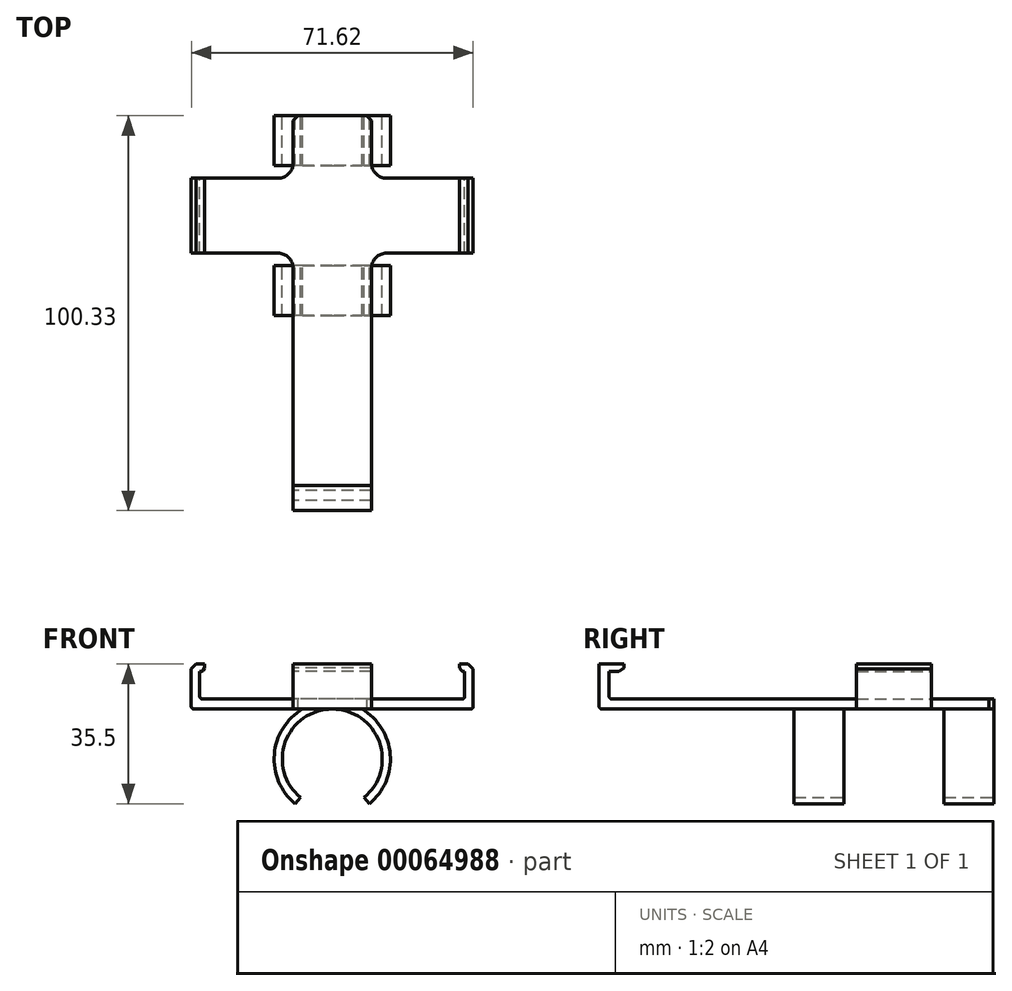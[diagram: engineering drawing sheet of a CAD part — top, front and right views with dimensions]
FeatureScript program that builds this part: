
annotation { "Feature Type Name" : "Feature", "Feature Type Description" : "" }
export const myFeature = defineFeature(function(context is Context, id is Id, definition is map)
    precondition{}
    {
        {
            var Q0;
            Q0=qCreatedBy(makeId("Front.planeOp"),FACE);
            var sketch = newSketch(context, id + "F0", { "sketchPlane" : qUnion([Q0])});
            skArc(sketch, "E0", {"start": v(9.41, -11.37) * mm, "mid": v(0, 14.76) * mm, "end": v(-9.41, -11.37) * mm});
            skArc(sketch, "E1", {"start": v(8.1, -9.78) * mm, "mid": v(0, 12.7) * mm, "end": v(-8.1, -9.78) * mm});
            skLineSegment(sketch, "E2", {"start": v(-8.1, -9.78) * mm, "end": v(-9.41, -11.37) * mm});
            skLineSegment(sketch, "E3", {"start": v(8.1, -9.78) * mm, "end": v(9.41, -11.37) * mm});
            skLineSegment(sketch, "E4", {"start": v(0, 0) * mm, "end": v(0, -14.76) * mm, "construction": true});
            skSolve(sketch);
        }
        {
            var Q0;
            Q0 = qSketchRegion(id + "F0", true);
            extrude(context, id + "F1", {"entities" : qUnion([Q0]), "depth" : 25.4 * mm, "hasSecondDirection" : true, "secondDirectionOppositeDirection" : true, "secondDirectionDepth" : 25.4 * mm});
        }
        {
            var Q0;
            Q0=qCreatedBy(makeId("Right.planeOp"),FACE);
            var sketch = newSketch(context, id + "F2", { "sketchPlane" : qUnion([Q0])});
            skLineSegment(sketch, "E5.bottom", {"start": v(-12.7, 21.65) * mm, "end": v(12.7, 21.65) * mm});
            skLineSegment(sketch, "E5.top", {"start": v(-12.7, -19.3) * mm, "end": v(12.7, -19.3) * mm});
            skLineSegment(sketch, "E5.left", {"start": v(-12.7, 21.65) * mm, "end": v(-12.7, -19.3) * mm});
            skLineSegment(sketch, "E5.right", {"start": v(12.7, 21.65) * mm, "end": v(12.7, -19.3) * mm});
            skSolve(sketch);
        }
        {
            var Q0;
            Q0 = qSketchRegion(id + "F2", true);
            extrude(context, id + "F3", {"entities" : qUnion([Q0]), "operationType" : NewBodyOperationType.REMOVE, "oppositeDirection" : true, "depth" : 25.4 * mm, "hasSecondDirection" : true, "secondDirectionOppositeDirection" : false, "secondDirectionDepth" : 25.4 * mm});
        }
        {
            var Q0;
            Q0=qCreatedBy(makeId("Front.planeOp"),FACE);
            var sketch = newSketch(context, id + "F4", { "sketchPlane" : qUnion([Q0])});
            skLineSegment(sketch, "E6", {"start": v(0, 12.7) * mm, "end": v(0, 14.76) * mm, "construction": true});
            skLineSegment(sketch, "E7.rect.bottom", {"start": v(9.97, 12.7) * mm, "end": v(-9.97, 12.7) * mm});
            skLineSegment(sketch, "E7.rect.top", {"start": v(9.97, 15.24) * mm, "end": v(-9.97, 15.24) * mm});
            skLineSegment(sketch, "E7.rect.left", {"start": v(9.97, 12.7) * mm, "end": v(9.97, 15.24) * mm});
            skLineSegment(sketch, "E7.rect.right", {"start": v(-9.97, 12.7) * mm, "end": v(-9.97, 15.24) * mm});
            skPoint(sketch, "E7.rect.middle", {"position": v(0, 13.97) * mm});
            skSolve(sketch);
        }
        {
            var Q0;
            Q0 = qSketchRegion(id + "F4", true);
            extrude(context, id + "F5", {"entities" : qUnion([Q0]), "operationType" : NewBodyOperationType.ADD, "depth" : 25.4 * mm, "hasSecondDirection" : true, "secondDirectionOppositeDirection" : true, "secondDirectionDepth" : 25.4 * mm});
        }
        {
            var Q0;
            Q0=qCreatedBy(makeId("Front.planeOp"),FACE);
            var sketch = newSketch(context, id + "F6", { "sketchPlane" : qUnion([Q0])});
            skLineSegment(sketch, "E8.rect.bottom", {"start": v(0, 12.7) * mm, "end": v(-33.66, 12.7) * mm});
            skLineSegment(sketch, "E8.rect.top", {"start": v(0, 15.24) * mm, "end": v(-33.02, 15.24) * mm});
            skPoint(sketch, "E8.rect.middle", {"position": v(0, 13.97) * mm});
            skLineSegment(sketch, "E9.bottom", {"start": v(-33.66, 12.7) * mm, "end": v(-35.18, 12.7) * mm});
            skLineSegment(sketch, "E9.left", {"start": v(-33.66, 15.87) * mm, "end": v(-33.65, 22.23) * mm});
            skLineSegment(sketch, "E9.right", {"start": v(-35.81, 13.33) * mm, "end": v(-35.81, 22.23) * mm});
            skPoint(sketch, "E10.visualSharp", {"position": v(-33.66, 15.24) * mm});
            skArc(sketch, "E10.filletArc", {"start": v(-33.66, 15.87) * mm, "mid": v(-33.47, 15.43) * mm, "end": v(-33.02, 15.24) * mm});
            skPoint(sketch, "E11.visualSharp", {"position": v(-35.81, 12.7) * mm});
            skArc(sketch, "E11.filletArc", {"start": v(-35.81, 13.33) * mm, "mid": v(-35.63, 12.89) * mm, "end": v(-35.18, 12.7) * mm});
            skLineSegment(sketch, "E12.bottom", {"start": v(-33.65, 22.23) * mm, "end": v(-33.36, 22.23) * mm});
            skLineSegment(sketch, "E12.top", {"start": v(-35.81, 24.13) * mm, "end": v(-32.39, 24.13) * mm});
            skLineSegment(sketch, "E12.left", {"start": v(-35.81, 22.23) * mm, "end": v(-35.81, 24.13) * mm});
            skLineSegment(sketch, "E12.right", {"start": v(-32.39, 23.18) * mm, "end": v(-32.39, 24.13) * mm});
            skLineSegment(sketch, "E13", {"start": v(-32.39, 23.18) * mm, "end": v(-32.83, 22.5) * mm});
            skPoint(sketch, "E14.orphan", {"position": v(-32.38, 22.23) * mm});
            skPoint(sketch, "E15.visualSharp", {"position": v(-33.02, 22.23) * mm});
            skArc(sketch, "E15.filletArc", {"start": v(-33.36, 22.23) * mm, "mid": v(-33.06, 22.3) * mm, "end": v(-32.83, 22.5) * mm});
            skLineSegment(sketch, "E16", {"start": v(0, 15.24) * mm, "end": v(0, 12.7) * mm});
            skLineSegment(sketch, "E17.MirrorCS", {"start": v(0, 15.24) * mm, "end": v(33.02, 15.24) * mm});
            skLineSegment(sketch, "E18.MirrorCS", {"start": v(0, 12.7) * mm, "end": v(33.66, 12.7) * mm});
            skLineSegment(sketch, "E19.MirrorCS", {"start": v(33.66, 12.7) * mm, "end": v(35.18, 12.7) * mm});
            skArc(sketch, "E20.MirrorCS", {"start": v(35.81, 13.33) * mm, "mid": v(35.63, 12.89) * mm, "end": v(35.18, 12.7) * mm});
            skLineSegment(sketch, "E21.MirrorCS", {"start": v(35.81, 13.33) * mm, "end": v(35.81, 22.22) * mm});
            skArc(sketch, "E22.MirrorCS", {"start": v(33.66, 15.87) * mm, "mid": v(33.47, 15.43) * mm, "end": v(33.02, 15.24) * mm});
            skLineSegment(sketch, "E23.MirrorCS", {"start": v(33.66, 15.87) * mm, "end": v(33.65, 22.22) * mm});
            skLineSegment(sketch, "E24.MirrorCS", {"start": v(35.81, 22.22) * mm, "end": v(35.81, 24.13) * mm});
            skLineSegment(sketch, "E25.MirrorCS", {"start": v(35.81, 24.13) * mm, "end": v(32.39, 24.13) * mm});
            skLineSegment(sketch, "E26.MirrorCS", {"start": v(32.39, 23.18) * mm, "end": v(32.39, 24.13) * mm});
            skLineSegment(sketch, "E27.MirrorCS", {"start": v(32.39, 23.18) * mm, "end": v(32.83, 22.5) * mm});
            skArc(sketch, "E28.MirrorCS", {"start": v(33.36, 22.22) * mm, "mid": v(33.06, 22.3) * mm, "end": v(32.83, 22.5) * mm});
            skLineSegment(sketch, "E29.MirrorCS", {"start": v(33.66, 22.22) * mm, "end": v(33.36, 22.22) * mm});
            skSolve(sketch);
        }
        {
            var Q0;
            Q0 = qSketchRegion(id + "F6", true);
            extrude(context, id + "F7", {"entities" : qUnion([Q0]), "operationType" : NewBodyOperationType.ADD, "depth" : 9.52 * mm, "hasSecondDirection" : true, "secondDirectionOppositeDirection" : true, "secondDirectionDepth" : 9.52 * mm});
        }
        {
            var Q0;
            Q0=makeQuery(id+"F7.boolean.opBoolean","INTERSECT",EDGE,{"derivedFrom":[makeQuery(id+"F5.opExtrude","SWEPT_FACE",FACE,{"disambiguationData":[OSD([sQuery(id+"F4.wireOp",EDGE,"E7.rect.right")])]}),makeQuery(id+"F7.opExtrude","CAP_FACE",FACE,{"disambiguationData":[OSD([sQuery(id+"F6.wireOp",EDGE,"E8.rect.bottom"),sQuery(id+"F6.wireOp",EDGE,"E8.rect.top"),sQuery(id+"F6.wireOp",EDGE,"E9.bottom"),sQuery(id+"F6.wireOp",EDGE,"E9.left"),sQuery(id+"F6.wireOp",EDGE,"E9.right"),sQuery(id+"F6.wireOp",EDGE,"E10.filletArc"),sQuery(id+"F6.wireOp",EDGE,"E11.filletArc"),sQuery(id+"F6.wireOp",EDGE,"E12.bottom"),sQuery(id+"F6.wireOp",EDGE,"E12.top"),sQuery(id+"F6.wireOp",EDGE,"E12.left"),sQuery(id+"F6.wireOp",EDGE,"E12.right"),sQuery(id+"F6.wireOp",EDGE,"E13"),sQuery(id+"F6.wireOp",EDGE,"E15.filletArc"),sQuery(id+"F6.wireOp",EDGE,"E17.MirrorCS"),sQuery(id+"F6.wireOp",EDGE,"E18.MirrorCS"),sQuery(id+"F6.wireOp",EDGE,"E19.MirrorCS"),sQuery(id+"F6.wireOp",EDGE,"E20.MirrorCS"),sQuery(id+"F6.wireOp",EDGE,"E21.MirrorCS"),sQuery(id+"F6.wireOp",EDGE,"E22.MirrorCS"),sQuery(id+"F6.wireOp",EDGE,"E23.MirrorCS"),sQuery(id+"F6.wireOp",EDGE,"E24.MirrorCS"),sQuery(id+"F6.wireOp",EDGE,"E25.MirrorCS"),sQuery(id+"F6.wireOp",EDGE,"E26.MirrorCS"),sQuery(id+"F6.wireOp",EDGE,"E27.MirrorCS"),sQuery(id+"F6.wireOp",EDGE,"E28.MirrorCS"),sQuery(id+"F6.wireOp",EDGE,"E29.MirrorCS")])],"isStart":true})]});
            var Q1;
            Q1=makeQuery(id+"F7.boolean.opBoolean","INTERSECT",EDGE,{"derivedFrom":[makeQuery(id+"F5.opExtrude","SWEPT_FACE",FACE,{"disambiguationData":[OSD([sQuery(id+"F4.wireOp",EDGE,"E7.rect.left")])]}),makeQuery(id+"F7.opExtrude","CAP_FACE",FACE,{"disambiguationData":[OSD([sQuery(id+"F6.wireOp",EDGE,"E8.rect.bottom"),sQuery(id+"F6.wireOp",EDGE,"E8.rect.top"),sQuery(id+"F6.wireOp",EDGE,"E9.bottom"),sQuery(id+"F6.wireOp",EDGE,"E9.left"),sQuery(id+"F6.wireOp",EDGE,"E9.right"),sQuery(id+"F6.wireOp",EDGE,"E10.filletArc"),sQuery(id+"F6.wireOp",EDGE,"E11.filletArc"),sQuery(id+"F6.wireOp",EDGE,"E12.bottom"),sQuery(id+"F6.wireOp",EDGE,"E12.top"),sQuery(id+"F6.wireOp",EDGE,"E12.left"),sQuery(id+"F6.wireOp",EDGE,"E12.right"),sQuery(id+"F6.wireOp",EDGE,"E13"),sQuery(id+"F6.wireOp",EDGE,"E15.filletArc"),sQuery(id+"F6.wireOp",EDGE,"E17.MirrorCS"),sQuery(id+"F6.wireOp",EDGE,"E18.MirrorCS"),sQuery(id+"F6.wireOp",EDGE,"E19.MirrorCS"),sQuery(id+"F6.wireOp",EDGE,"E20.MirrorCS"),sQuery(id+"F6.wireOp",EDGE,"E21.MirrorCS"),sQuery(id+"F6.wireOp",EDGE,"E22.MirrorCS"),sQuery(id+"F6.wireOp",EDGE,"E23.MirrorCS"),sQuery(id+"F6.wireOp",EDGE,"E24.MirrorCS"),sQuery(id+"F6.wireOp",EDGE,"E25.MirrorCS"),sQuery(id+"F6.wireOp",EDGE,"E26.MirrorCS"),sQuery(id+"F6.wireOp",EDGE,"E27.MirrorCS"),sQuery(id+"F6.wireOp",EDGE,"E28.MirrorCS"),sQuery(id+"F6.wireOp",EDGE,"E29.MirrorCS")])],"isStart":true})]});
            var Q2;
            Q2=makeQuery(id+"F7.boolean.opBoolean","INTERSECT",EDGE,{"derivedFrom":[makeQuery(id+"F5.opExtrude","SWEPT_FACE",FACE,{"disambiguationData":[OSD([sQuery(id+"F4.wireOp",EDGE,"E7.rect.left")])]}),makeQuery(id+"F7.opExtrude","CAP_FACE",FACE,{"disambiguationData":[OSD([sQuery(id+"F6.wireOp",EDGE,"E8.rect.bottom"),sQuery(id+"F6.wireOp",EDGE,"E8.rect.top"),sQuery(id+"F6.wireOp",EDGE,"E9.bottom"),sQuery(id+"F6.wireOp",EDGE,"E9.left"),sQuery(id+"F6.wireOp",EDGE,"E9.right"),sQuery(id+"F6.wireOp",EDGE,"E10.filletArc"),sQuery(id+"F6.wireOp",EDGE,"E11.filletArc"),sQuery(id+"F6.wireOp",EDGE,"E12.bottom"),sQuery(id+"F6.wireOp",EDGE,"E12.top"),sQuery(id+"F6.wireOp",EDGE,"E12.left"),sQuery(id+"F6.wireOp",EDGE,"E12.right"),sQuery(id+"F6.wireOp",EDGE,"E13"),sQuery(id+"F6.wireOp",EDGE,"E15.filletArc"),sQuery(id+"F6.wireOp",EDGE,"E17.MirrorCS"),sQuery(id+"F6.wireOp",EDGE,"E18.MirrorCS"),sQuery(id+"F6.wireOp",EDGE,"E19.MirrorCS"),sQuery(id+"F6.wireOp",EDGE,"E20.MirrorCS"),sQuery(id+"F6.wireOp",EDGE,"E21.MirrorCS"),sQuery(id+"F6.wireOp",EDGE,"E22.MirrorCS"),sQuery(id+"F6.wireOp",EDGE,"E23.MirrorCS"),sQuery(id+"F6.wireOp",EDGE,"E24.MirrorCS"),sQuery(id+"F6.wireOp",EDGE,"E25.MirrorCS"),sQuery(id+"F6.wireOp",EDGE,"E26.MirrorCS"),sQuery(id+"F6.wireOp",EDGE,"E27.MirrorCS"),sQuery(id+"F6.wireOp",EDGE,"E28.MirrorCS"),sQuery(id+"F6.wireOp",EDGE,"E29.MirrorCS")])],"isStart":false})]});
            var Q3;
            Q3=makeQuery(id+"F7.boolean.opBoolean","INTERSECT",EDGE,{"derivedFrom":[makeQuery(id+"F5.opExtrude","SWEPT_FACE",FACE,{"disambiguationData":[OSD([sQuery(id+"F4.wireOp",EDGE,"E7.rect.right")])]}),makeQuery(id+"F7.opExtrude","CAP_FACE",FACE,{"disambiguationData":[OSD([sQuery(id+"F6.wireOp",EDGE,"E8.rect.bottom"),sQuery(id+"F6.wireOp",EDGE,"E8.rect.top"),sQuery(id+"F6.wireOp",EDGE,"E9.bottom"),sQuery(id+"F6.wireOp",EDGE,"E9.left"),sQuery(id+"F6.wireOp",EDGE,"E9.right"),sQuery(id+"F6.wireOp",EDGE,"E10.filletArc"),sQuery(id+"F6.wireOp",EDGE,"E11.filletArc"),sQuery(id+"F6.wireOp",EDGE,"E12.bottom"),sQuery(id+"F6.wireOp",EDGE,"E12.top"),sQuery(id+"F6.wireOp",EDGE,"E12.left"),sQuery(id+"F6.wireOp",EDGE,"E12.right"),sQuery(id+"F6.wireOp",EDGE,"E13"),sQuery(id+"F6.wireOp",EDGE,"E15.filletArc"),sQuery(id+"F6.wireOp",EDGE,"E17.MirrorCS"),sQuery(id+"F6.wireOp",EDGE,"E18.MirrorCS"),sQuery(id+"F6.wireOp",EDGE,"E19.MirrorCS"),sQuery(id+"F6.wireOp",EDGE,"E20.MirrorCS"),sQuery(id+"F6.wireOp",EDGE,"E21.MirrorCS"),sQuery(id+"F6.wireOp",EDGE,"E22.MirrorCS"),sQuery(id+"F6.wireOp",EDGE,"E23.MirrorCS"),sQuery(id+"F6.wireOp",EDGE,"E24.MirrorCS"),sQuery(id+"F6.wireOp",EDGE,"E25.MirrorCS"),sQuery(id+"F6.wireOp",EDGE,"E26.MirrorCS"),sQuery(id+"F6.wireOp",EDGE,"E27.MirrorCS"),sQuery(id+"F6.wireOp",EDGE,"E28.MirrorCS"),sQuery(id+"F6.wireOp",EDGE,"E29.MirrorCS")])],"isStart":false})]});
            fillet(context, id + "F8", {"entities" : qUnion([Q0, Q1, Q2, Q3]), "radius" : 3.8 * mm, "tangentPropagation" : true, "allowEdgeOverflow" : false});
        }
        {
            var Q0;
            Q0=qCreatedBy(makeId("Right.planeOp"),FACE);
            var sketch = newSketch(context, id + "F9", { "sketchPlane" : qUnion([Q0])});
            skLineSegment(sketch, "E30.bottom", {"start": v(0, 12.7) * mm, "end": v(-72.4, 12.7) * mm});
            skLineSegment(sketch, "E30.top", {"start": v(0, 15.24) * mm, "end": v(-71.76, 15.24) * mm});
            skLineSegment(sketch, "E30.left", {"start": v(0, 12.7) * mm, "end": v(0, 15.24) * mm});
            skLineSegment(sketch, "E31.bottom", {"start": v(-72.4, 12.7) * mm, "end": v(-74.3, 12.7) * mm});
            skLineSegment(sketch, "E31.top", {"start": v(-72.4, 24.13) * mm, "end": v(-74.93, 24.13) * mm});
            skLineSegment(sketch, "E31.left", {"start": v(-72.4, 15.88) * mm, "end": v(-72.4, 22.23) * mm});
            skLineSegment(sketch, "E31.right", {"start": v(-74.93, 13.33) * mm, "end": v(-74.93, 24.13) * mm});
            skLineSegment(sketch, "E32.bottom", {"start": v(-74.93, 24.13) * mm, "end": v(-68.58, 24.13) * mm});
            skLineSegment(sketch, "E32.top", {"start": v(-72.4, 22.23) * mm, "end": v(-69.85, 22.23) * mm});
            skLineSegment(sketch, "E32.right", {"start": v(-68.58, 24.13) * mm, "end": v(-68.58, 23.18) * mm});
            skLineSegment(sketch, "E33", {"start": v(-68.58, 23.18) * mm, "end": v(-69.85, 22.23) * mm});
            skPoint(sketch, "E34.orphan", {"position": v(-68.58, 22.23) * mm});
            skPoint(sketch, "E35.visualSharp", {"position": v(-72.4, 15.24) * mm});
            skArc(sketch, "E35.filletArc", {"start": v(-72.4, 15.88) * mm, "mid": v(-72.2, 15.43) * mm, "end": v(-71.76, 15.24) * mm});
            skPoint(sketch, "E36.visualSharp", {"position": v(-74.93, 12.7) * mm});
            skArc(sketch, "E36.filletArc", {"start": v(-74.93, 13.33) * mm, "mid": v(-74.74, 12.89) * mm, "end": v(-74.3, 12.7) * mm});
            skSolve(sketch);
        }
        {
            var Q0;
            Q0 = qSketchRegion(id + "F9", true);
            var Q1;
            {var subQ2=sQuery(id+"F4.wireOp",EDGE,"E7.rect.left");Q1=makeQuery(id+"F7.boolean.opBoolean","SPLIT",FACE,{"disambiguationData":[TD([makeQuery(id+"F1.opExtrude","CAP_FACE",FACE,{"disambiguationData":[OSD([sQuery(id+"F0.wireOp",EDGE,"E0"),sQuery(id+"F0.wireOp",EDGE,"E1"),sQuery(id+"F0.wireOp",EDGE,"E2"),sQuery(id+"F0.wireOp",EDGE,"E3")])],"isStart":false})])],"derivedFrom":makeQuery(id+"F5.opExtrude","SWEPT_FACE",FACE,{"disambiguationData":[OSD([subQ2])]})});}
            var Q2;
            {var subQ2=sQuery(id+"F4.wireOp",EDGE,"E7.rect.right");Q2=makeQuery(id+"F7.boolean.opBoolean","SPLIT",FACE,{"disambiguationData":[TD([makeQuery(id+"F1.opExtrude","CAP_FACE",FACE,{"disambiguationData":[OSD([sQuery(id+"F0.wireOp",EDGE,"E0"),sQuery(id+"F0.wireOp",EDGE,"E1"),sQuery(id+"F0.wireOp",EDGE,"E2"),sQuery(id+"F0.wireOp",EDGE,"E3")])],"isStart":false})])],"derivedFrom":makeQuery(id+"F5.opExtrude","SWEPT_FACE",FACE,{"disambiguationData":[OSD([subQ2])]})});}
            extrude(context, id + "F10", {"entities" : qUnion([Q0]), "operationType" : NewBodyOperationType.ADD, "endBound" : BoundingType.UP_TO_SURFACE, "endBoundEntityFace" : qUnion([Q1]), "depth" : 10.16 * mm, "hasSecondDirection" : true, "secondDirectionBound" : SecondDirectionBoundingType.UP_TO_SURFACE, "secondDirectionOppositeDirection" : true, "secondDirectionBoundEntityFace" : qUnion([Q2]), "secondDirectionDepth" : 6.35 * mm});
        }
        {
            var Q0;
            Q0=makeQuery(id+"F5.opExtrude","CAP_EDGE",EDGE,{"disambiguationData":[OSD([sQuery(id+"F4.wireOp",EDGE,"E7.rect.right")])],"isStart":true});
            var Q1;
            Q1=makeQuery(id+"F5.opExtrude","CAP_EDGE",EDGE,{"disambiguationData":[OSD([sQuery(id+"F4.wireOp",EDGE,"E7.rect.left")])],"isStart":true});
            chamfer(context, id + "F11", {"entities" : qUnion([Q0, Q1]), "width" : 1.27 * mm, "tangentPropagation" : true});
        }
        {
            var Q0;
            {var subQ0=sQuery(id+"F9.wireOp",EDGE,"E32.bottom");var subQ1=sQuery(id+"F9.wireOp",EDGE,"E31.right");Q0=makeQuery(id+"F10.opExtrude","TWEAK_EDGE",EDGE,{"derivedFrom":[makeQuery(id+"F9.imprint","IMPRINT",EDGE,{"derivedFrom":subQ1}),makeQuery(id+"F9.imprint","IMPRINT",EDGE,{"disambiguationData":[TD([[makeQuery(id+"F9.imprint","INTERSECT",VERTEX,{"derivedFrom":[subQ1,subQ0]}),-1.0]])],"derivedFrom":subQ0})]});}
            var Q1;
            Q1=makeQuery(id+"F7.opExtrude","SWEPT_EDGE",EDGE,{"disambiguationData":[OSD([sQuery(id+"F6.wireOp",EDGE,"E12.top"),sQuery(id+"F6.wireOp",EDGE,"E12.left")])]});
            var Q2;
            Q2=makeQuery(id+"F7.opExtrude","SWEPT_EDGE",EDGE,{"disambiguationData":[OSD([sQuery(id+"F6.wireOp",EDGE,"E24.MirrorCS"),sQuery(id+"F6.wireOp",EDGE,"E25.MirrorCS")])]});
            chamfer(context, id + "F12", {"entities" : qUnion([Q0, Q1, Q2]), "width" : 1.27 * mm, "tangentPropagation" : true});
        }
    });
